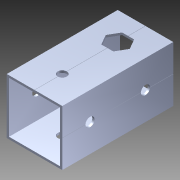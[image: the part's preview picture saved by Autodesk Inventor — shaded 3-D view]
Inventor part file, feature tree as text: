
AUTODESK INVENTOR PART (.ipt)
format: ipt  version: 2014 (Build 180170000, 170)  size: 1,181,184 bytes
history: native  units: in
note: dims shown in document units (in); Inventor stores cm internally (conversion verified against a paired STEP export)
features: extrude x2, sketch x2, pattern_circular x1, other x1, plane x1, imported_body x1
ambient origin geometry x8: Origin, YZ Plane, XZ Plane, XY Plane, X Axis, Y Axis, Z Axis, Center Point
bodies: Body1 (feature_tree)
feature tree (8):
  pattern_circular  "CirPattern2"
  other  "217-3426-STEP1"
  plane  "Work Plane1"
  extrude  "Extrusion1"  Depth=3937.0079in TaperAngle=0.0deg
  extrude  "Extrusion2"  Depth=2.0in TaperAngle=0.0deg
  imported_body  "Base1"
  sketch  "Sketch1"  dims[d0=-2.0in d1=3937.0079in d2=0.0in]
  sketch  "Sketch3"  dims[d3=0.375in d4=2.0in d5=0.0in]
